FCSTD DOCUMENT  (FreeCAD 0.21R33771 (Git))
Label: tc2-touch-sensor
License: All rights reserved
LicenseURL: https://en.wikipedia.org/wiki/All_rights_reserved
objects: Sketcher::SketchObject×1
note: 1 computed .brp shape members not serialized (recipe doc carries the construction recipe); baked Part::Feature solids carry a one-line shape summary decoded from their .brp

FEATURE [Sketcher::SketchObject] Sketch  label="Boarder"
  FullyConstrained = true
  sketch-geometry (13):
    g0: LineSegment StartX=-20.5 StartY=9.5 StartZ=0 EndX=28 EndY=9.5 EndZ=0
    g1: LineSegment StartX=28 StartY=9.5 StartZ=0 EndX=28 EndY=-7.8 EndZ=0
    g2: LineSegment StartX=28 StartY=-7.8 StartZ=0 EndX=12 EndY=-7.8 EndZ=0
    g3: LineSegment StartX=12 StartY=-7.8 StartZ=0 EndX=12 EndY=-7 EndZ=0
    g4: LineSegment StartX=11 StartY=-6 StartZ=0 EndX=-4 EndY=-6 EndZ=0
    g5: LineSegment StartX=-5 StartY=-7 StartZ=0 EndX=-5 EndY=-7.8 EndZ=0
    g6: LineSegment StartX=-5 StartY=-7.8 StartZ=0 EndX=-22.6 EndY=-7.8 EndZ=0
    g7: LineSegment StartX=-22.6 StartY=-7.8 StartZ=0 EndX=-22.6 EndY=1 EndZ=0
    g8: LineSegment StartX=-22.6 StartY=1 StartZ=0 EndX=-21.5 EndY=1 EndZ=0
    g9: LineSegment StartX=-20.5 StartY=2 StartZ=0 EndX=-20.5 EndY=9.5 EndZ=0
    g10: ArcOfCircle CenterX=-21.5 CenterY=2 CenterZ=0 NormalX=0 NormalY=0 NormalZ=1 AngleXU=0 Radius=1 StartAngle=4.71239 EndAngle=6.28319
    g11: ArcOfCircle CenterX=-4 CenterY=-7 CenterZ=0 NormalX=0 NormalY=0 NormalZ=1 AngleXU=0 Radius=1 StartAngle=1.5708 EndAngle=3.14159
    g12: ArcOfCircle CenterX=11 CenterY=-7 CenterZ=0 NormalX=0 NormalY=0 NormalZ=1 AngleXU=0 Radius=1 StartAngle=0 EndAngle=1.5708
  constraints (36):
    c: Horizontal(g0)
    c: Coincident(g0,g1)
    c: Vertical(g1)
    c: Coincident(g1,g2)
    c: Horizontal(g2)
    c: Coincident(g2,g3)
    c: Horizontal(g4)
    c: Coincident(g5,g6)
    c: Horizontal(g6)
    c: Coincident(g6,g7)
    c: Coincident(g7,g8)
    c: Coincident(g9,g0)
    c: Vertical(g9)
    c: Vertical(g7)
    c: Vertical(g5)
    c: Horizontal(g8)
    c: DistanceX(g-1,g0) = 28
    c: DistanceY(g-1,g0) = 9.5
    c: DistanceY(g1,g1) = 17.3
    c: Vertical(g3)
    c: Horizontal(g5,g2)
    c: DistanceX(g6,g1) = 50.6
    c: DistanceX(g7,g0) = 2.1
    c: DistanceY(g7,g0) = 8.5
    c: DistanceX(g2,g2) = 16
    c: Tangent(g8,g10) = -1.5708
    c: Tangent(g9,g10) = -1.5708
    c: Tangent(g4,g11) = -1.5708
    c: Tangent(g5,g11) = -1.5708
    c: Tangent(g3,g12) = -1.5708
    c: Tangent(g4,g12) = -1.5708
    c: Equal(g11,g12)
    c: Equal(g11,g10)
    c: Radius(g11) = 1
    c: DistanceX(g5,g2) = 17
    c: DistanceY(g5,g4) = 1.8
